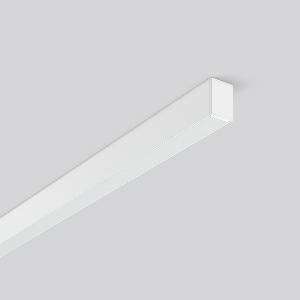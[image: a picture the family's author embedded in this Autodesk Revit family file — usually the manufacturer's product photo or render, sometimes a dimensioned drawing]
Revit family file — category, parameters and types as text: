
# Revit family: less_is_more_27_312197_002_1147
name_source: partatom
category: Lighting Fixtures
units: mm (PartAtom-declared; Revit-internal decimal feet)

## family parameters
Cut with Voids When Loaded = No
Host = Face
Light Source = No
Part Type = Normal
Room Calculation Point = No
Round Connector Dimension = Use Diameter
Shared = No

## types (1)
- LESS IS MORE 27 (1 x LED Modul 830, 2150 lm, 3000)
    Apparent Load = 29 VA
    CIE Flux Codes = 65 89 98 100 100
    Color Rendering = 80
    Color Temperature = 3000
    Default Elevation = 1800 mm
    Description = Series: LESS IS MORE 27
Ceiling luminaire with slim design. Housing: extruded aluminium profile, powder-coated. End cap aluminium powder-coated. Diffuser made of non-yellowing plastic (PMMA) microprismatic. Suitable for Ceiling mounting, Wall (surface). External driver with connecting cable. 
Colour: traffic white, matt (RAL 9016)
Length: 1012 mm
Width: 28 mm
Height: 38 mm
Lamp: LED
Socket: without socket
Colour temperature: 3000K
Colour rendering index (CRI): 82
System power: 29 W
Rated luminous flux: 2150 lm
Luminous efficiency: 74 lm/W
Control gear: Regulated power supply
Protection class: II
Type of protection: IP 20
    Height = 38 mm
    Lamp = 1 x LED Modul 830
    Lamp Light Flux = 2150 lm
    Lamp count = 1
    Length = 1012 mm
    Lifetime = 50000 h
    Luminous efficacy = 74 lm/W
    Manufacturer = RZB
    ModVariant = No
    Model = 312197.002
    Mounting Place = Ceiling, Wall
    Mounting Type = Surface mounted
    Number of Poles = 1
    OnlyDefault = Yes
    Power Factor = 1
    Product Name = LESS IS MORE 27
    Product group = Surface mounted LED linear luminaires
    ProductGroupID = 307
    Protection Class = Protection class II
    Protection Degree = IP 20
    RLX_Detail_Level = 1
    RLX_Emergency_Light_Flux = 0 lm
    RLX_Emergency_Type = 0
    RLX_Emergency_Type_DB = No
    RlxData = <blob elided: 24021 chars, md5=0c2f7389>
    Socket = socket
    Standby Power = 0 W
    System Light Flux = 2150 lm
    System Power = 29 W
    Type Comments = Product without accessories
    Type Image = 312196.002.jpg
    URL = http://relux.com
    VarID = ---
    Voltage = 230 V
    Voltage Range = 220-240 V
    Weight = 0.00 kg
    Width = 28 mm

## geometry (parser evidence)
native form markers: Blend x4, Sweep x11
no freeform markers — native parametric forms only
